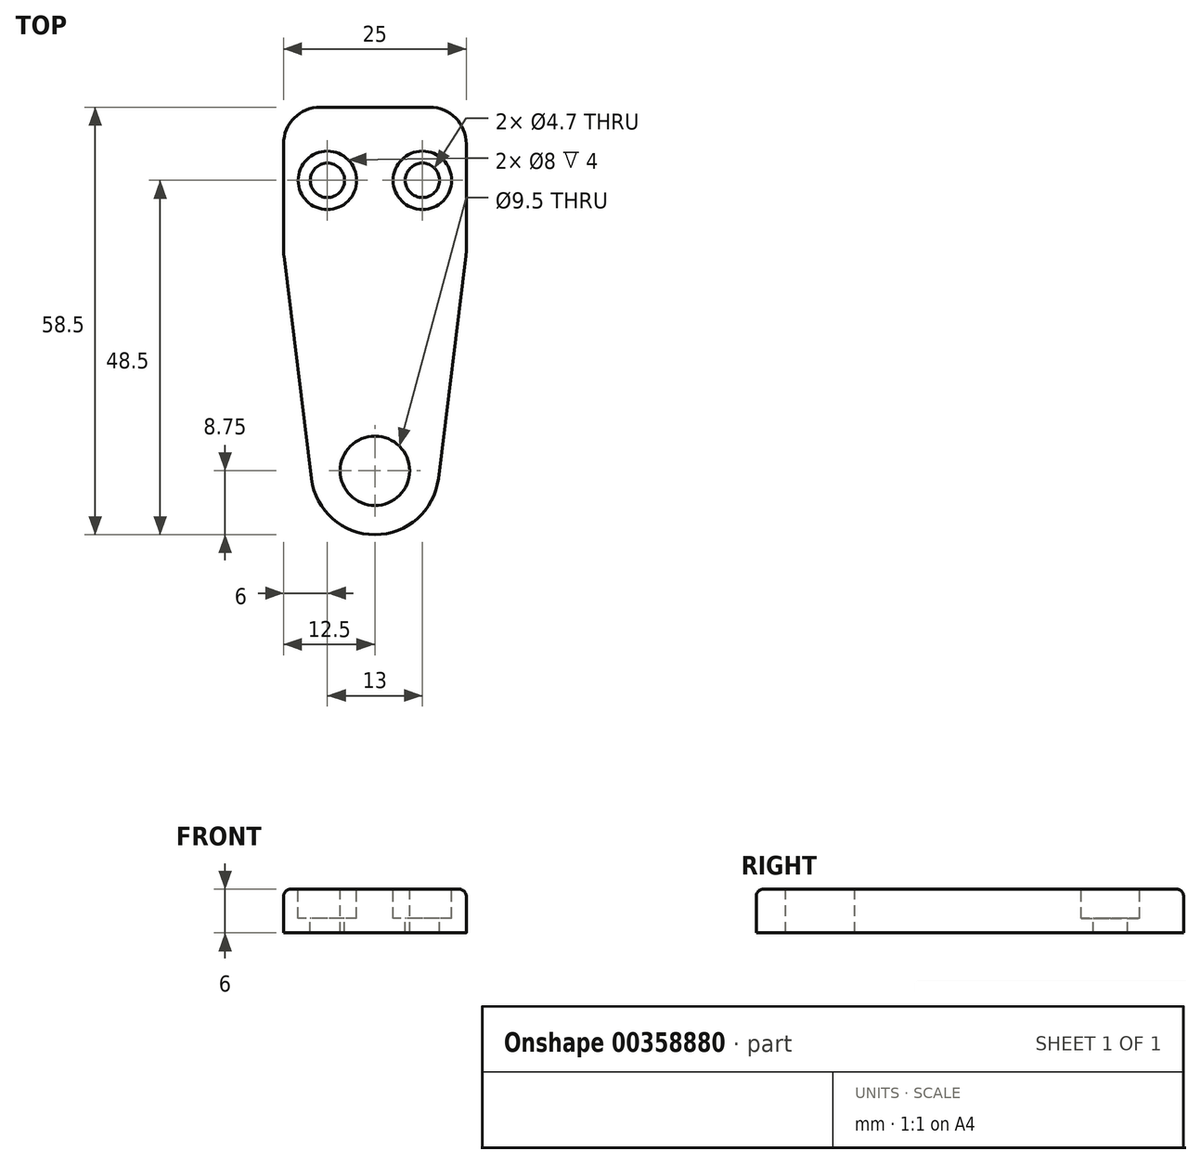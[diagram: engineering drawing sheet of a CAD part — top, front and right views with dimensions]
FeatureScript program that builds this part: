
annotation { "Feature Type Name" : "Feature", "Feature Type Description" : "" }
export const myFeature = defineFeature(function(context is Context, id is Id, definition is map)
    precondition{}
    {
        {
            var Q0;
            Q0=qCreatedBy(makeId("Top.planeOp"),FACE);
            var sketch = newSketch(context, id + "F0", { "sketchPlane" : qUnion([Q0])});
            skLineSegment(sketch, "E0.top", {"start": v(-12.5, 49.75) * mm, "end": v(12.5, 49.75) * mm});
            skCircle(sketch, "E1", {"center": v(0, 0) * mm, "radius": 4.75 * mm});
            skCircle(sketch, "E2", {"center": v(-6.5, 39.75) * mm, "radius": 2.35 * mm});
            skCircle(sketch, "E3", {"center": v(6.5, 39.75) * mm, "radius": 2.35 * mm});
            skCircle(sketch, "E4", {"center": v(-6.5, 39.75) * mm, "radius": 4 * mm});
            skCircle(sketch, "E5", {"center": v(6.5, 39.75) * mm, "radius": 4 * mm});
            skLineSegment(sketch, "E6", {"start": v(-6.5, 39.75) * mm, "end": v(-12.5, 39.75) * mm, "construction": true});
            skLineSegment(sketch, "E7", {"start": v(6.5, 39.75) * mm, "end": v(12.5, 39.75) * mm, "construction": true});
            skArc(sketch, "E8", {"start": v(-8.68, -1.08) * mm, "mid": v(0, -8.75) * mm, "end": v(8.68, -1.08) * mm});
            skLineSegment(sketch, "E9", {"start": v(-12.5, 49.75) * mm, "end": v(-12.5, 29.75) * mm});
            skLineSegment(sketch, "E10", {"start": v(-12.5, 29.75) * mm, "end": v(-8.68, -1.08) * mm});
            skLineSegment(sketch, "E11", {"start": v(12.5, 49.75) * mm, "end": v(12.5, 29.75) * mm});
            skLineSegment(sketch, "E12", {"start": v(12.5, 29.75) * mm, "end": v(8.68, -1.08) * mm});
            skSolve(sketch);
        }
        {
            var Q0;
            Q0 = qSketchRegion(id + "F0", true);
            var Q1;
            Q1=makeQuery(id+"F0.imprint","IMPRINT",FACE,{"disambiguationData":[TD([[makeQuery(id+"F0.imprint","IMPRINT",EDGE,{"derivedFrom":sQuery(id+"F0.wireOp",EDGE,"E2")}),-1.0]])]});
            var Q2;
            Q2=makeQuery(id+"F0.imprint","IMPRINT",FACE,{"disambiguationData":[TD([[makeQuery(id+"F0.imprint","IMPRINT",EDGE,{"derivedFrom":sQuery(id+"F0.wireOp",EDGE,"E3")}),-1.0]])]});
            extrude(context, id + "F1", {"entities" : qUnion([Q0, Q1, Q2]), "oppositeDirection" : true, "depth" : 6 * mm, "offsetDistance" : 25 * mm});
        }
        {
            var Q0;
            Q0=makeQuery(id+"F0.imprint","IMPRINT",FACE,{"disambiguationData":[TD([[makeQuery(id+"F0.imprint","IMPRINT",EDGE,{"derivedFrom":sQuery(id+"F0.wireOp",EDGE,"E2")}),-1.0]])]});
            var Q1;
            Q1=makeQuery(id+"F0.imprint","IMPRINT",FACE,{"disambiguationData":[TD([[makeQuery(id+"F0.imprint","IMPRINT",EDGE,{"derivedFrom":sQuery(id+"F0.wireOp",EDGE,"E3")}),-1.0]])]});
            extrude(context, id + "F2", {"entities" : qUnion([Q0, Q1]), "operationType" : NewBodyOperationType.REMOVE, "oppositeDirection" : true, "depth" : 4 * mm, "offsetDistance" : 25 * mm});
        }
        {
            var Q0;
            Q0=makeQuery(id+"F1.opExtrude","SWEPT_EDGE",EDGE,{"disambiguationData":[OSD([sQuery(id+"F0.wireOp",EDGE,"E0.top"),sQuery(id+"F0.wireOp",EDGE,"E9")])]});
            var Q1;
            Q1=makeQuery(id+"F1.opExtrude","SWEPT_EDGE",EDGE,{"disambiguationData":[OSD([sQuery(id+"F0.wireOp",EDGE,"E0.top"),sQuery(id+"F0.wireOp",EDGE,"E11")])]});
            var Q2;
            Q2=makeQuery(id+"F1.opExtrude","SWEPT_EDGE",EDGE,{"disambiguationData":[OSD([sQuery(id+"F0.wireOp",EDGE,"E9"),sQuery(id+"F0.wireOp",EDGE,"E10")])]});
            var Q3;
            Q3=makeQuery(id+"F1.opExtrude","SWEPT_EDGE",EDGE,{"disambiguationData":[OSD([sQuery(id+"F0.wireOp",EDGE,"E11"),sQuery(id+"F0.wireOp",EDGE,"E12")])]});
            fillet(context, id + "F3", {"entities" : qUnion([Q0, Q1, Q2, Q3]), "tangentPropagation" : true, "radius" : 5 * mm, "defaultsChanged" : false, "vertexSettings" : [], "allowEdgeOverflow" : false});
        }
        {
            var Q0;
            Q0=makeQuery(id+"F1.opExtrude","CAP_EDGE",EDGE,{"disambiguationData":[OSD([sQuery(id+"F0.wireOp",EDGE,"E10")])],"isStart":true});
            fillet(context, id + "F4", {"entities" : qUnion([Q0]), "tangentPropagation" : true, "radius" : 1 * mm, "defaultsChanged" : true, "vertexSettings" : [], "allowEdgeOverflow" : false});
        }
    });
